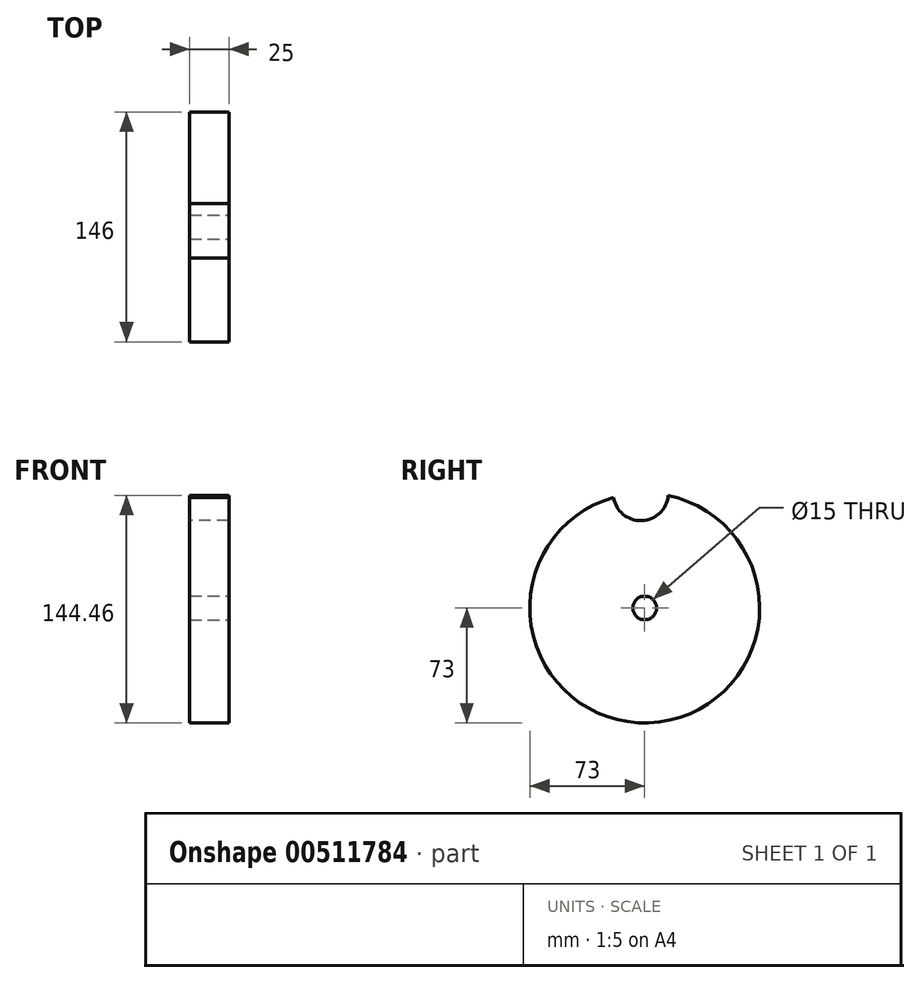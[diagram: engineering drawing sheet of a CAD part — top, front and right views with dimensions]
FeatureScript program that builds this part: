
annotation { "Feature Type Name" : "Feature", "Feature Type Description" : "" }
export const myFeature = defineFeature(function(context is Context, id is Id, definition is map)
    precondition{}
    {
        {
            var Q0;
            Q0=qCreatedBy(makeId("Right.planeOp"),FACE);
            var sketch = newSketch(context, id + "F0", { "sketchPlane" : qUnion([Q0])});
            skCircle(sketch, "E0", {"center": v(0, 0) * mm, "radius": 73 * mm});
            skPoint(sketch, "E1", {"position": v(-2.51, 72.96) * mm});
            skSolve(sketch);
        }
        {
            var Q0;
            Q0=makeQuery(id+"F0.imprint","IMPRINT",FACE,{"disambiguationData":[TD([[makeQuery(id+"F0.imprint","IMPRINT",EDGE,{"derivedFrom":sQuery(id+"F0.wireOp",EDGE,"E0")}),1.0]])]});
            extrude(context, id + "F1", {"entities" : qUnion([Q0]), "depth" : 25 * mm});
        }
        {
            var Q0;
            Q0=makeQuery(id+"F1.opExtrude","CAP_FACE",FACE,{"disambiguationData":[OSD([sQuery(id+"F0.wireOp",EDGE,"E0")])],"isStart":false});
            var sketch = newSketch(context, id + "F2", { "sketchPlane" : qUnion([Q0])});
            skCircle(sketch, "E2", {"center": v(0, 0) * mm, "radius": 25 * mm});
            skSolve(sketch);
        }
        {
            var Q0;
            Q0=sQuery(id+"F0.wireOp",VERTEX,"E0.center");
            var Q1;
            Q1=sQuery(id+"F2.wireOp",VERTEX,"E2.center");
            var Q2;
            Q2=makeQuery(id+"F1.opExtrude","SWEPT_BODY",BODY,{"disambiguationData":[OSD([sQuery(id+"F0.wireOp",EDGE,"E0")])]});
            hole(context, id + "F3", {"style" : HoleStyle.SIMPLE, "endStyle" : HoleEndStyle.THROUGH, "holeDiameter" : 15 * mm, "isTappedThrough" : true, "tappedDepth" : 12 * mm, "tapClearance" : 3, "locations" : qUnion([Q0, Q1]), "scope" : qUnion([Q2])});
        }
        {
            var Q0;
            Q0=makeQuery(id+"F1.opExtrude","SWEPT_BODY",BODY,{"disambiguationData":[OSD([sQuery(id+"F0.wireOp",EDGE,"E0")])]});
            transform(context, id + "F4", {"entities" : qUnion([Q0]), "transformType" : TransformType.TRANSLATION_3D, "dx" : 0 * mm, "dy" : 0 * mm, "dz" : 0 * mm, "makeCopy" : true});
        }
        {
            var Q0;
            Q0=makeQuery(id+"F4.opPattern","COPY",BODY,{"derivedFrom":makeQuery(id+"F1.opExtrude","SWEPT_BODY",BODY,{"disambiguationData":[OSD([sQuery(id+"F0.wireOp",EDGE,"E0")])]}),"instanceName":"1"});
            deleteBodies(context, id + "F5", {"entities" : qUnion([Q0])});
        }
        {
            var Q0;
            Q0=makeQuery(id+"F1.opExtrude","SWEPT_BODY",BODY,{"disambiguationData":[OSD([sQuery(id+"F0.wireOp",EDGE,"E0")])]});
            transform(context, id + "F6", {"entities" : qUnion([Q0]), "transformType" : TransformType.TRANSLATION_3D, "dx" : 0 * mm, "dy" : -287 * mm, "dz" : 0 * mm, "makeCopy" : true});
        }
        {
            var Q0;
            Q0=makeQuery(id+"F6.opPattern","COPY",BODY,{"derivedFrom":makeQuery(id+"F1.opExtrude","SWEPT_BODY",BODY,{"disambiguationData":[OSD([sQuery(id+"F0.wireOp",EDGE,"E0")])]}),"instanceName":"1"});
            deleteBodies(context, id + "F7", {"entities" : qUnion([Q0])});
        }
        {
            var Q0;
            Q0=makeQuery(id+"F1.opExtrude","SWEPT_BODY",BODY,{"disambiguationData":[OSD([sQuery(id+"F0.wireOp",EDGE,"E0")])]});
            transform(context, id + "F8", {"entities" : qUnion([Q0]), "transformType" : TransformType.TRANSLATION_3D, "dx" : 385 * mm, "dy" : 0 * mm, "dz" : 0 * mm, "makeCopy" : true});
        }
        {
            var Q0;
            Q0=makeQuery(id+"F8.opPattern","COPY",BODY,{"derivedFrom":makeQuery(id+"F1.opExtrude","SWEPT_BODY",BODY,{"disambiguationData":[OSD([sQuery(id+"F0.wireOp",EDGE,"E0")])]}),"instanceName":"1"});
            deleteBodies(context, id + "F9", {"entities" : qUnion([Q0])});
        }
        {
            var Q0;
            Q0=sQuery(id+"F0.wireOp",VERTEX,"E1");
            var Q1;
            Q1=makeQuery(id+"F1.opExtrude","SWEPT_BODY",BODY,{"disambiguationData":[OSD([sQuery(id+"F0.wireOp",EDGE,"E0")])]});
            hole(context, id + "F10", {"style" : HoleStyle.SIMPLE, "endStyle" : HoleEndStyle.THROUGH, "oppositeDirection" : true, "holeDiameter" : 35 * mm, "isTappedThrough" : true, "tappedDepth" : 12 * mm, "tapClearance" : 3, "locations" : qUnion([Q0]), "scope" : qUnion([Q1])});
        }
    });
